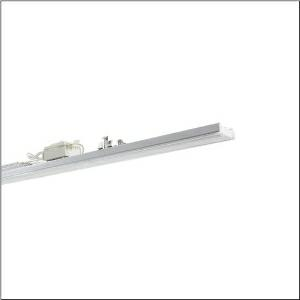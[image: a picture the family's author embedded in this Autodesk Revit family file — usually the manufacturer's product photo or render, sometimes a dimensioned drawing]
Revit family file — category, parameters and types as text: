
# Revit family: licross_r__21_recessed_ho_52tl11dn4e5s_92ad
name_source: partatom
category: Lighting Fixtures
units: mm (PartAtom-declared; Revit-internal decimal feet)

## family parameters
Cut with Voids When Loaded = No
Host = Face
Light Source = No
Part Type = Normal
Room Calculation Point = No
Round Connector Dimension = Use Diameter
Shared = No

## types (1)
- --- (1 x LED, 14970 lm, 84.6 W, 4000K)
    Apparent Load = 85 VA
    CIE Flux Codes = 87 95 99 100 100
    Color Rendering = 80
    Color Temperature = 4000K
    Default Elevation = 1800 mm
    Description = Licross® 21 Recessed HO, luminaire insert, of sheet steel, galvanised, coil coated, white, length: 1.500mm, width: 66mm, height: 67mm, LED rated luminous flux: 14.970lm, light colour: 840, control gear: DALI 2, with plug, 5-pole, with phase selection, mains connection: 220..240V, AC, 50/60Hz, rated input power: 85W, halogen-free wiring, primary light control with lens, of plastic, primary optical cover: cover, of PMMA, light emission: direct distribution, primary light characteristic: symmetric, protection rating (complete): IP40, insulation class (complete): insulation class I (protective earthing), certification: CE, ENEC, VDE, UKCA, protection symbol: D if used in an environment without relevant dust loads with corresponding accessories, impact resistance: IK06, permissible ambient temperature for indoor applications: -25..+30°C, corresponds to IFS (International Featured Standards) requirements for safety and quality in the food industry, reducing of maximum allowable ambient temperature of 5°C with ceiling mounting, LABS conformity tested according to VDMA 24364:2018-05, packaging unit: 1 piece
    Height = 58 mm
    Lamp = 1 x LED
    Lamp Light Flux = 14970 lm
    Lamp Power = 84.6 W
    Lamp count = 1
    Length = 1500 mm
    Luminous efficacy = 177 lm/W
    Manufacturer = Siteco
    ModVariant = No
    Model = 52TL11DN4E5S
    Mounting Place = Ceiling
    Mounting Type = Pendant
    Number of Poles = 1
    OnlyDefault = Yes
    Power Factor = 1
    Product Name = Licross® 21 Recessed HO
    Product group = luminaire insert
    ProductGroupID = 902
    Protection Class = Protection class I
    Protection Degree = IP 40
    RLX_Detail_Level = 1
    RLX_Emergency_Light_Flux = 0 lm
    RLX_Emergency_Type = 0
    RLX_Emergency_Type_DB = No
    RlxData = <blob elided: 24613 chars, md5=dcf5a47f>
    Socket = socket
    Standby Power = 0 W
    System Light Flux = 14970 lm
    System Power = 85 W
    Type Comments = factory setting: luminous flux: 100 % | dim-lin: 254 | 484 mA
    Type Image = l_1296930.jpg
    URL = http://relux.com
    VarID = @adj_127294
    Voltage = 0 V
    Weight = 0.00 kg
    Width = 66 mm

## geometry (parser evidence)
native form markers: Blend x4, Sweep x12
no freeform markers — native parametric forms only
